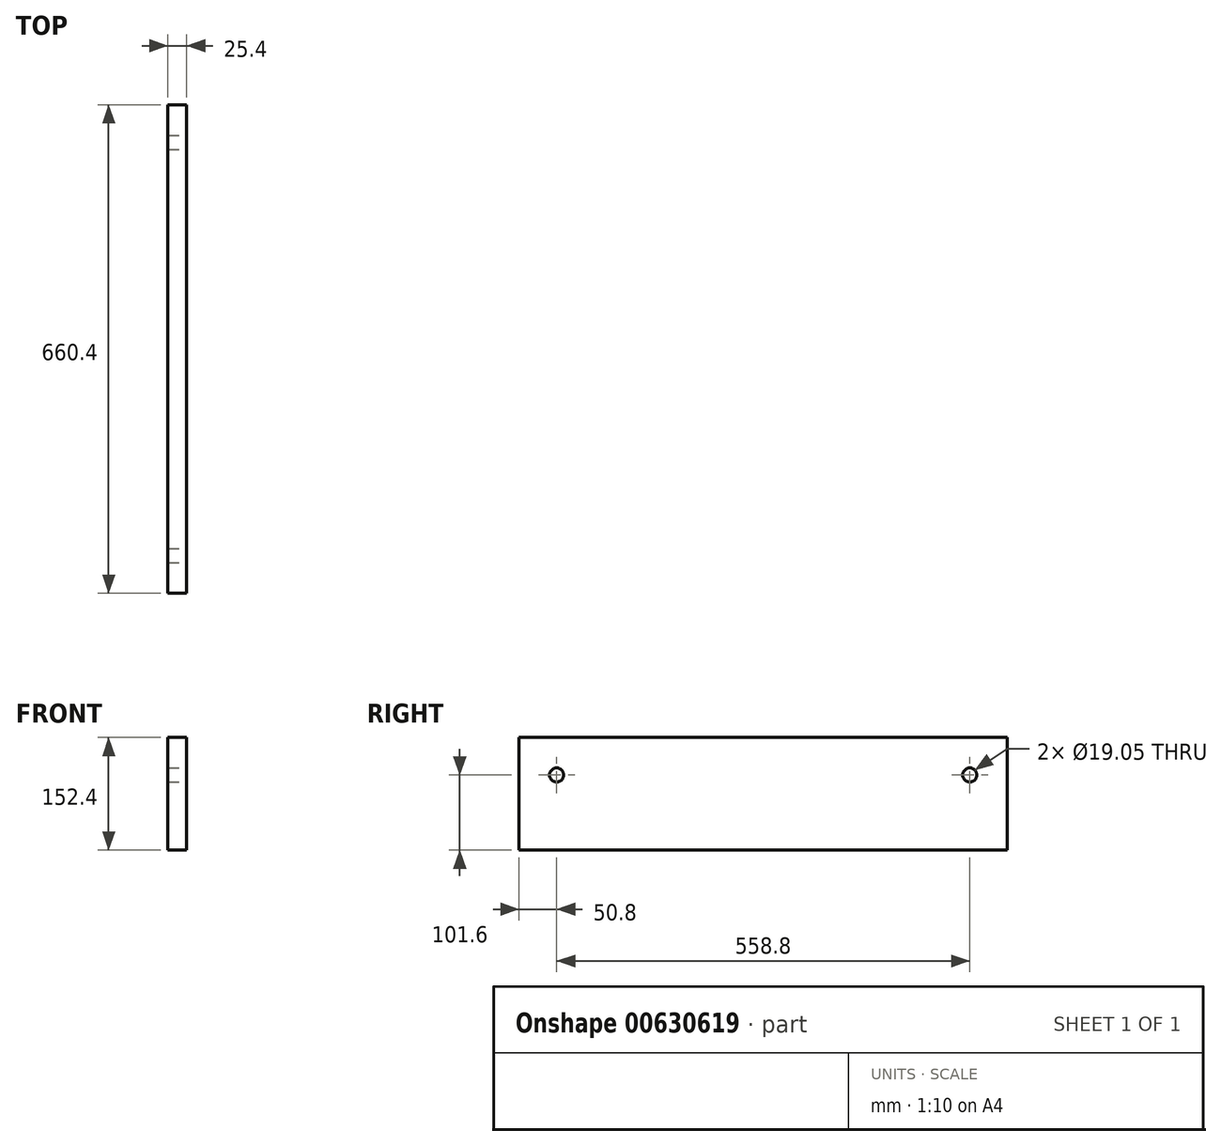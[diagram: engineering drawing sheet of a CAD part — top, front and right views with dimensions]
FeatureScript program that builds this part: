
annotation { "Feature Type Name" : "Feature", "Feature Type Description" : "" }
export const myFeature = defineFeature(function(context is Context, id is Id, definition is map)
    precondition{}
    {
        {
            var Q0;
            Q0=qCreatedBy(makeId("Front.planeOp"),FACE);
            var sketch = newSketch(context, id + "F0", { "sketchPlane" : qUnion([Q0])});
            skLineSegment(sketch, "E0.bottom", {"start": v(12.7, 76.2) * mm, "end": v(-12.7, 76.2) * mm});
            skLineSegment(sketch, "E0.top", {"start": v(12.7, -76.2) * mm, "end": v(-12.7, -76.2) * mm});
            skLineSegment(sketch, "E0.left", {"start": v(12.7, 76.2) * mm, "end": v(12.7, -76.2) * mm});
            skLineSegment(sketch, "E0.right", {"start": v(-12.7, 76.2) * mm, "end": v(-12.7, -76.2) * mm});
            skPoint(sketch, "E0.middle", {"position": v(0, 0) * mm});
            skSolve(sketch);
        }
        {
            var Q0;
            Q0=makeQuery(id+"F0.imprint","IMPRINT",FACE,{"disambiguationData":[TD([[makeQuery(id+"F0.imprint","IMPRINT",EDGE,{"derivedFrom":sQuery(id+"F0.wireOp",EDGE,"E0.bottom")}),1.0]])]});
            extrude(context, id + "F1", {"entities" : qUnion([Q0]), "depth" : 660.4 * mm, "offsetDistance" : 25.4 * mm});
        }
        {
            var Q0;
            Q0=makeQuery(id+"F1.opExtrude","SWEPT_FACE",FACE,{"disambiguationData":[OSD([sQuery(id+"F0.wireOp",EDGE,"E0.left")])]});
            var sketch = newSketch(context, id + "F2", { "sketchPlane" : qUnion([Q0])});
            skCircle(sketch, "E1", {"center": v(-609.6, 25.4) * mm, "radius": 9.53 * mm});
            skCircle(sketch, "E2", {"center": v(-50.8, 25.4) * mm, "radius": 9.53 * mm});
            skSolve(sketch);
        }
        {
            var Q0;
            Q0=makeQuery(id+"F2.imprint","IMPRINT",FACE,{"disambiguationData":[TD([[makeQuery(id+"F2.imprint","IMPRINT",EDGE,{"derivedFrom":sQuery(id+"F2.wireOp",EDGE,"E1")}),1.0]])]});
            var Q1;
            Q1=makeQuery(id+"F2.imprint","IMPRINT",FACE,{"disambiguationData":[TD([[makeQuery(id+"F2.imprint","IMPRINT",EDGE,{"derivedFrom":sQuery(id+"F2.wireOp",EDGE,"E2")}),1.0]])]});
            extrude(context, id + "F3", {"entities" : qUnion([Q0, Q1]), "operationType" : NewBodyOperationType.REMOVE, "endBound" : BoundingType.THROUGH_ALL, "oppositeDirection" : true, "depth" : 25.4 * mm, "offsetDistance" : 25.4 * mm});
        }
    });
